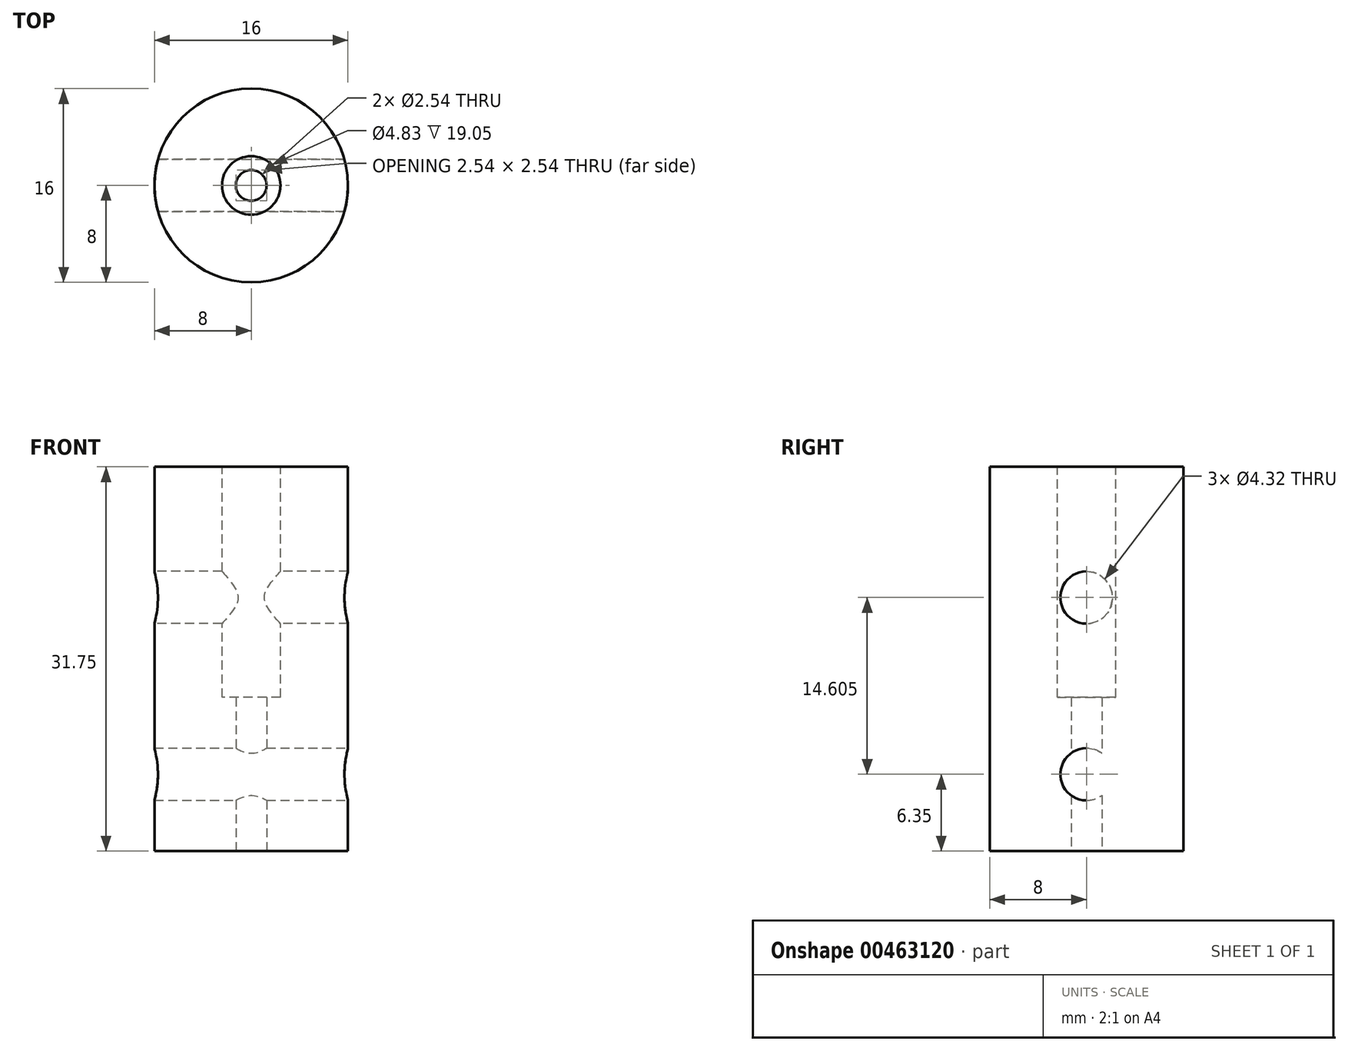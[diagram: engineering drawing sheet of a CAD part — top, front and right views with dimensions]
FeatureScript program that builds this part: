
annotation { "Feature Type Name" : "Feature", "Feature Type Description" : "" }
export const myFeature = defineFeature(function(context is Context, id is Id, definition is map)
    precondition{}
    {
        {
            var Q0;
            Q0=qCreatedBy(makeId("Top.planeOp"),FACE);
            var sketch = newSketch(context, id + "F0", { "sketchPlane" : qUnion([Q0])});
            skCircle(sketch, "E0", {"center": v(0, 0) * mm, "radius": 8 * mm});
            skCircle(sketch, "E1", {"center": v(0, 0) * mm, "radius": 1.27 * mm});
            skSolve(sketch);
        }
        {
            var Q0;
            Q0=makeQuery(id+"F0.imprint","IMPRINT",FACE,{"disambiguationData":[TD([[makeQuery(id+"F0.imprint","IMPRINT",EDGE,{"derivedFrom":sQuery(id+"F0.wireOp",EDGE,"E0")}),1.0]])]});
            extrude(context, id + "F1", {"entities" : qUnion([Q0]), "depth" : 31.75 * mm});
        }
        {
            var Q0;
            Q0=makeQuery(id+"F1.opExtrude","CAP_FACE",FACE,{"disambiguationData":[OSD([sQuery(id+"F0.wireOp",EDGE,"E0"),sQuery(id+"F0.wireOp",EDGE,"E1")])],"isStart":false});
            var sketch = newSketch(context, id + "F2", { "sketchPlane" : qUnion([Q0])});
            skCircle(sketch, "E2", {"center": v(0, 0) * mm, "radius": 2.41 * mm});
            skSolve(sketch);
        }
        {
            var Q0;
            Q0=makeQuery(id+"F2.imprint","IMPRINT",FACE,{"disambiguationData":[TD([[makeQuery(id+"F2.imprint","IMPRINT",EDGE,{"derivedFrom":sQuery(id+"F2.wireOp",EDGE,"E2")}),1.0]])]});
            extrude(context, id + "F3", {"entities" : qUnion([Q0]), "operationType" : NewBodyOperationType.REMOVE, "oppositeDirection" : true, "depth" : 19.05 * mm});
        }
        {
            var Q0;
            Q0=qCreatedBy(makeId("Right.planeOp"),FACE);
            var sketch = newSketch(context, id + "F4", { "sketchPlane" : qUnion([Q0])});
            skCircle(sketch, "E3", {"center": v(0, 6.35) * mm, "radius": 2.16 * mm});
            skCircle(sketch, "E4", {"center": v(0, 20.96) * mm, "radius": 2.16 * mm});
            skSolve(sketch);
        }
        {
            var Q0;
            Q0=makeQuery(id+"F4.imprint","IMPRINT",FACE,{"disambiguationData":[TD([[makeQuery(id+"F4.imprint","IMPRINT",EDGE,{"derivedFrom":sQuery(id+"F4.wireOp",EDGE,"E4")}),1.0]])]});
            extrude(context, id + "F5", {"entities" : qUnion([Q0]), "operationType" : NewBodyOperationType.REMOVE, "endBound" : BoundingType.SYMMETRIC, "depth" : 25.4 * mm});
        }
        {
            var Q0;
            Q0=makeQuery(id+"F4.imprint","IMPRINT",FACE,{"disambiguationData":[TD([[makeQuery(id+"F4.imprint","IMPRINT",EDGE,{"derivedFrom":sQuery(id+"F4.wireOp",EDGE,"E3")}),1.0]])]});
            extrude(context, id + "F6", {"entities" : qUnion([Q0]), "operationType" : NewBodyOperationType.REMOVE, "endBound" : BoundingType.SYMMETRIC, "oppositeDirection" : true, "depth" : 25.4 * mm});
        }
    });
